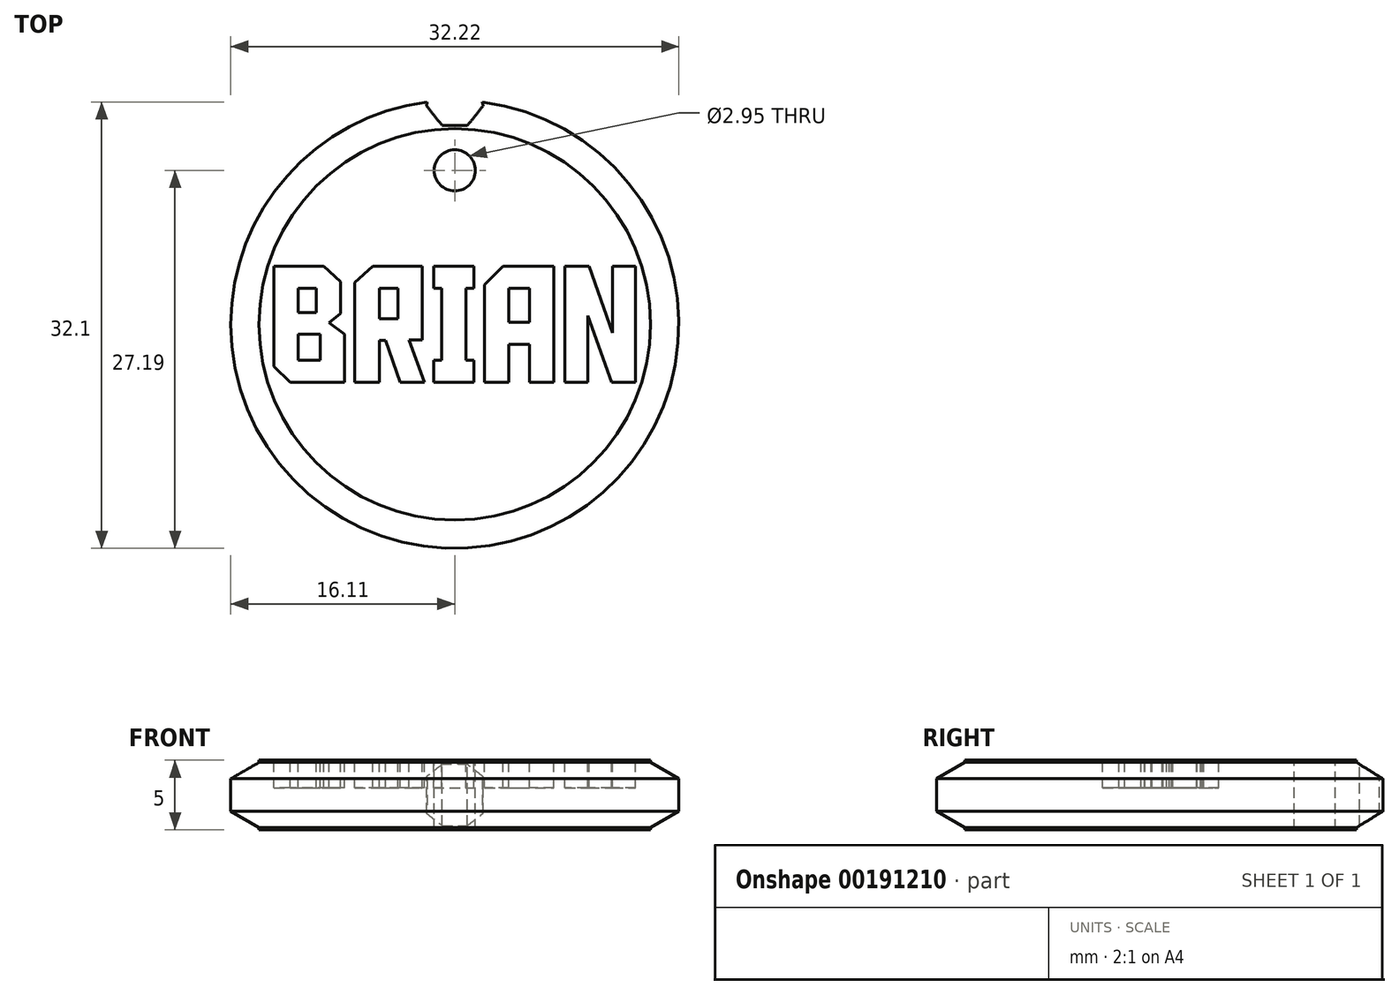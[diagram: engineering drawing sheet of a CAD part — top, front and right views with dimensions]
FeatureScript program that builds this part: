
annotation { "Feature Type Name" : "Feature", "Feature Type Description" : "" }
export const myFeature = defineFeature(function(context is Context, id is Id, definition is map)
    precondition{}
    {
        {
            var Q0;
            Q0=qCreatedBy(makeId("Front.planeOp"),FACE);
            var sketch = newSketch(context, id + "F0", { "sketchPlane" : qUnion([Q0])});
            skLineSegment(sketch, "E0.bottom", {"start": v(0, 0) * mm, "end": v(-14.08, 0) * mm});
            skLineSegment(sketch, "E0.top", {"start": v(0, 5) * mm, "end": v(-14.08, 5) * mm});
            skLineSegment(sketch, "E0.left", {"start": v(0, 0) * mm, "end": v(0, 5) * mm});
            skLineSegment(sketch, "E0.right", {"start": v(-14.08, 0) * mm, "end": v(-14.08, 5) * mm});
            skArc(sketch, "E1.cCircle", {"start": v(-13.06, 4.26) * mm, "mid": v(-16.1, 2.5) * mm, "end": v(-13.06, 0.74) * mm, "construction": true});
            skLineSegment(sketch, "E1.1", {"start": v(-13.06, 0.74) * mm, "end": v(-14.08, 0.16) * mm});
            skLineSegment(sketch, "E1.2", {"start": v(-14.08, 0.16) * mm, "end": v(-16.1, 1.33) * mm});
            skLineSegment(sketch, "E1.3", {"start": v(-16.1, 1.33) * mm, "end": v(-16.1, 3.67) * mm});
            skLineSegment(sketch, "E1.4", {"start": v(-16.1, 3.67) * mm, "end": v(-14.08, 4.84) * mm});
            skLineSegment(sketch, "E1.5", {"start": v(-14.08, 4.84) * mm, "end": v(-13.06, 4.26) * mm});
            skPoint(sketch, "E1.0.midPoint", {"position": v(-12.05, 2.5) * mm});
            skPoint(sketch, "E2.orphan", {"position": v(-12.05, 1.33) * mm});
            skPoint(sketch, "E3.orphan", {"position": v(-12.05, 3.67) * mm});
            skSolve(sketch);
        }
        {
            var Q0;
            Q0 = qSketchRegion(id + "F0", true);
            var Q1;
            Q1=sQuery(id+"F0.wireOp",EDGE,"E0.left");
            revolve(context, id + "F1", {"entities" : qUnion([Q0]), "axis" : qUnion([Q1]), "revolveType" : RevolveType.FULL});
        }
        {
            var Q0;
            Q0=qCreatedBy(makeId("Top.planeOp"),FACE);
            cPlane(context, id + "F2", {"entities" : qUnion([Q0]), "cplaneType" : CPlaneType.OFFSET, "offset" : 7 * mm, "width" : 152.4 * mm, "height" : 152.4 * mm});
        }
        {
            var Q0;
            Q0=qCreatedBy(id+"F2.planeOp",FACE);
            var sketch = newSketch(context, id + "F3", { "sketchPlane" : qUnion([Q0])});
            skCircle(sketch, "E4.cCircle", {"center": v(0, 16.19) * mm, "radius": 1.88 * mm, "construction": true});
            skLineSegment(sketch, "E4.0", {"start": v(0.9, 14.3) * mm, "end": v(-0.9, 14.3) * mm});
            skLineSegment(sketch, "E4.1", {"start": v(-0.9, 14.3) * mm, "end": v(-2.04, 15.72) * mm});
            skLineSegment(sketch, "E4.2", {"start": v(-2.04, 15.72) * mm, "end": v(-1.63, 17.5) * mm});
            skLineSegment(sketch, "E4.3", {"start": v(-1.63, 17.5) * mm, "end": v(0, 18.28) * mm});
            skLineSegment(sketch, "E4.4", {"start": v(0, 18.28) * mm, "end": v(1.63, 17.5) * mm});
            skLineSegment(sketch, "E4.5", {"start": v(1.63, 17.5) * mm, "end": v(2.04, 15.72) * mm});
            skLineSegment(sketch, "E4.6", {"start": v(2.04, 15.72) * mm, "end": v(0.9, 14.3) * mm});
            skPoint(sketch, "E4.0.midPoint", {"position": v(0, 14.3) * mm});
            skSolve(sketch);
        }
        {
            var Q0;
            Q0 = qSketchRegion(id + "F3", true);
            extrude(context, id + "F4", {"entities" : qUnion([Q0]), "operationType" : NewBodyOperationType.REMOVE, "oppositeDirection" : true, "depth" : 25.4 * mm});
        }
        {
            var Q0;
            Q0=qCreatedBy(id+"F2.planeOp",FACE);
            var sketch = newSketch(context, id + "F5", { "sketchPlane" : qUnion([Q0])});
            skCircle(sketch, "E5", {"center": v(0, 11.08) * mm, "radius": 1.48 * mm});
            skSolve(sketch);
        }
        {
            var Q0;
            Q0 = qSketchRegion(id + "F5", true);
            extrude(context, id + "F6", {"entities" : qUnion([Q0]), "operationType" : NewBodyOperationType.REMOVE, "oppositeDirection" : true, "depth" : 25.4 * mm});
        }
        {
            var Q0;
            Q0=qCreatedBy(id+"F2.planeOp",FACE);
            var sketch = newSketch(context, id + "F7", { "sketchPlane" : qUnion([Q0])});
            skLineSegment(sketch, "E6", {"start": v(-7.92, -0.7) * mm, "end": v(-7.92, -4.18) * mm});
            skLineSegment(sketch, "E7", {"start": v(-7.92, -4.18) * mm, "end": v(-11.84, -4.18) * mm});
            skLineSegment(sketch, "E8", {"start": v(-11.84, -4.18) * mm, "end": v(-13, -3.02) * mm});
            skLineSegment(sketch, "E9", {"start": v(-13, -3.02) * mm, "end": v(-13, 4.18) * mm});
            skLineSegment(sketch, "E10", {"start": v(-13, 4.18) * mm, "end": v(-9.42, 4.18) * mm});
            skLineSegment(sketch, "E11", {"start": v(-9.42, 4.18) * mm, "end": v(-8.23, 3.08) * mm});
            skLineSegment(sketch, "E12", {"start": v(-8.23, 3.08) * mm, "end": v(-8.23, 0.77) * mm});
            skLineSegment(sketch, "E13", {"start": v(-8.23, 0.77) * mm, "end": v(-9.05, 0.12) * mm});
            skLineSegment(sketch, "E14", {"start": v(-9.05, 0.12) * mm, "end": v(-7.92, -0.7) * mm});
            skLineSegment(sketch, "E15", {"start": v(-9.68, -2.6) * mm, "end": v(-9.68, -0.7) * mm});
            skLineSegment(sketch, "E16", {"start": v(-9.68, -0.7) * mm, "end": v(-11.25, -0.7) * mm});
            skLineSegment(sketch, "E17", {"start": v(-11.25, -0.7) * mm, "end": v(-11.25, -2.6) * mm});
            skLineSegment(sketch, "E18", {"start": v(-11.25, -2.6) * mm, "end": v(-9.68, -2.6) * mm});
            skLineSegment(sketch, "E19", {"start": v(-9.97, 0.86) * mm, "end": v(-9.97, 2.59) * mm});
            skLineSegment(sketch, "E20", {"start": v(-9.97, 2.59) * mm, "end": v(-11.25, 2.59) * mm});
            skLineSegment(sketch, "E21", {"start": v(-11.25, 2.59) * mm, "end": v(-11.25, 0.86) * mm});
            skLineSegment(sketch, "E22", {"start": v(-11.25, 0.86) * mm, "end": v(-9.97, 0.86) * mm});
            skLineSegment(sketch, "E23", {"start": v(-3.93, -4.18) * mm, "end": v(-4.97, -1.16) * mm});
            skLineSegment(sketch, "E24", {"start": v(-4.97, -1.16) * mm, "end": v(-5.43, -1.16) * mm});
            skLineSegment(sketch, "E25", {"start": v(-5.43, -1.16) * mm, "end": v(-5.43, -4.18) * mm});
            skLineSegment(sketch, "E26", {"start": v(-5.43, -4.18) * mm, "end": v(-7.18, -4.18) * mm});
            skLineSegment(sketch, "E27", {"start": v(-7.18, -4.18) * mm, "end": v(-7.18, 3) * mm});
            skLineSegment(sketch, "E28", {"start": v(-7.18, 3) * mm, "end": v(-5.91, 4.18) * mm});
            skLineSegment(sketch, "E29", {"start": v(-5.91, 4.18) * mm, "end": v(-2.34, 4.18) * mm});
            skLineSegment(sketch, "E30", {"start": v(-2.34, 4.18) * mm, "end": v(-2.34, -1.13) * mm});
            skLineSegment(sketch, "E31", {"start": v(-2.34, -1.13) * mm, "end": v(-3.28, -1.13) * mm});
            skLineSegment(sketch, "E32", {"start": v(-3.28, -1.13) * mm, "end": v(-2.17, -4.18) * mm});
            skLineSegment(sketch, "E33", {"start": v(-2.17, -4.18) * mm, "end": v(-3.93, -4.18) * mm});
            skLineSegment(sketch, "E34", {"start": v(-4.09, 0.41) * mm, "end": v(-4.09, 2.59) * mm});
            skLineSegment(sketch, "E35", {"start": v(-4.09, 2.59) * mm, "end": v(-5.43, 2.59) * mm});
            skLineSegment(sketch, "E36", {"start": v(-5.43, 2.59) * mm, "end": v(-5.43, 0.41) * mm});
            skLineSegment(sketch, "E37", {"start": v(-5.43, 0.41) * mm, "end": v(-4.09, 0.41) * mm});
            skLineSegment(sketch, "E38", {"start": v(1.38, -2.6) * mm, "end": v(1.38, -4.18) * mm});
            skLineSegment(sketch, "E39", {"start": v(1.38, -4.18) * mm, "end": v(-1.53, -4.18) * mm});
            skLineSegment(sketch, "E40", {"start": v(-1.53, -4.18) * mm, "end": v(-1.53, -2.6) * mm});
            skLineSegment(sketch, "E41", {"start": v(-1.53, -2.6) * mm, "end": v(-0.95, -2.6) * mm});
            skLineSegment(sketch, "E42", {"start": v(-0.95, -2.6) * mm, "end": v(-0.95, 2.6) * mm});
            skLineSegment(sketch, "E43", {"start": v(-0.95, 2.6) * mm, "end": v(-1.53, 2.6) * mm});
            skLineSegment(sketch, "E44", {"start": v(-1.53, 2.6) * mm, "end": v(-1.53, 4.18) * mm});
            skLineSegment(sketch, "E45", {"start": v(-1.53, 4.18) * mm, "end": v(1.38, 4.18) * mm});
            skLineSegment(sketch, "E46", {"start": v(1.38, 4.18) * mm, "end": v(1.38, 2.6) * mm});
            skLineSegment(sketch, "E47", {"start": v(1.38, 2.6) * mm, "end": v(0.8, 2.6) * mm});
            skLineSegment(sketch, "E48", {"start": v(0.8, 2.6) * mm, "end": v(0.8, -2.6) * mm});
            skLineSegment(sketch, "E49", {"start": v(0.8, -2.6) * mm, "end": v(1.38, -2.6) * mm});
            skLineSegment(sketch, "E50", {"start": v(3.9, -4.18) * mm, "end": v(2.13, -4.18) * mm});
            skLineSegment(sketch, "E51", {"start": v(2.13, -4.18) * mm, "end": v(2.13, 2.86) * mm});
            skLineSegment(sketch, "E52", {"start": v(2.13, 2.86) * mm, "end": v(3.48, 4.18) * mm});
            skLineSegment(sketch, "E53", {"start": v(3.48, 4.18) * mm, "end": v(7.13, 4.18) * mm});
            skLineSegment(sketch, "E54", {"start": v(7.13, 4.18) * mm, "end": v(7.13, -4.18) * mm});
            skLineSegment(sketch, "E55", {"start": v(7.13, -4.18) * mm, "end": v(5.38, -4.18) * mm});
            skLineSegment(sketch, "E56", {"start": v(5.38, -4.18) * mm, "end": v(5.38, -1.43) * mm});
            skLineSegment(sketch, "E57", {"start": v(5.38, -1.43) * mm, "end": v(3.9, -1.43) * mm});
            skLineSegment(sketch, "E58", {"start": v(3.9, -1.43) * mm, "end": v(3.9, -4.18) * mm});
            skLineSegment(sketch, "E59", {"start": v(5.38, 0.16) * mm, "end": v(5.38, 2.59) * mm});
            skLineSegment(sketch, "E60", {"start": v(5.38, 2.59) * mm, "end": v(3.9, 2.59) * mm});
            skLineSegment(sketch, "E61", {"start": v(3.9, 2.59) * mm, "end": v(3.9, 0.16) * mm});
            skLineSegment(sketch, "E62", {"start": v(3.9, 0.16) * mm, "end": v(5.38, 0.16) * mm});
            skLineSegment(sketch, "E63", {"start": v(11.35, -0.62) * mm, "end": v(11.35, 4.18) * mm});
            skLineSegment(sketch, "E64", {"start": v(11.35, 4.18) * mm, "end": v(13, 4.18) * mm});
            skLineSegment(sketch, "E65", {"start": v(13, 4.18) * mm, "end": v(13, -4.18) * mm});
            skLineSegment(sketch, "E66", {"start": v(13, -4.18) * mm, "end": v(11.27, -4.18) * mm});
            skLineSegment(sketch, "E67", {"start": v(11.27, -4.18) * mm, "end": v(9.55, 0.62) * mm});
            skLineSegment(sketch, "E68", {"start": v(9.55, 0.62) * mm, "end": v(9.55, -4.18) * mm});
            skLineSegment(sketch, "E69", {"start": v(9.55, -4.18) * mm, "end": v(7.91, -4.18) * mm});
            skLineSegment(sketch, "E70", {"start": v(7.91, -4.18) * mm, "end": v(7.91, 4.18) * mm});
            skLineSegment(sketch, "E71", {"start": v(7.91, 4.18) * mm, "end": v(9.65, 4.18) * mm});
            skLineSegment(sketch, "E72", {"start": v(9.65, 4.18) * mm, "end": v(11.35, -0.62) * mm});
            skSolve(sketch);
        }
        {
            var Q0;
            Q0 = qSketchRegion(id + "F7", true);
            extrude(context, id + "F8", {"entities" : qUnion([Q0]), "operationType" : NewBodyOperationType.REMOVE, "oppositeDirection" : true, "depth" : 4 * mm});
        }
    });
